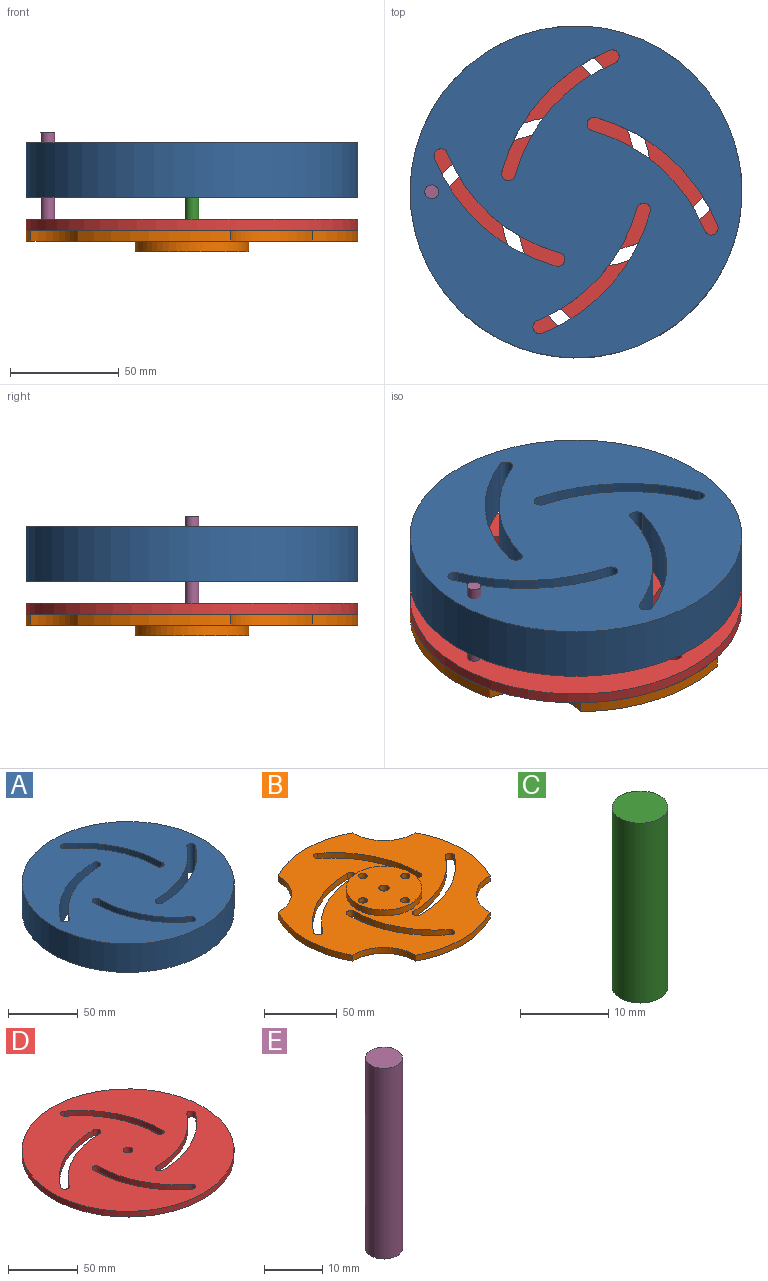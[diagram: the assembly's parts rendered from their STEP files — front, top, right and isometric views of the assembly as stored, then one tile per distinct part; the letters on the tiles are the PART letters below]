
ASSEMBLY  parts=5 mates=4
PART A: 19 faces, bbox 152.4x152.4x25 mm
  f0: plane 152.4x152.4mm, normal (0,0,1), area 16223.8mm2, adj f2,f3,f4,f5,f6,f7,f8,f9
  f1: plane 152.4x152.4mm, normal (0,0,-1), area 16223.8mm2, adj f2,f3,f4,f5,f6,f7,f8,f9
  f2: cylinder r=76.2mm len=152.4mm, axis (0,0,-1), area 11969.5mm2, adj f0,f1
  f3: cylinder r=83.46mm len=66.74mm, axis (0,0,1), area 1934.2mm2, adj f0,f1,f4,f6
  f4: cylinder r=3.18mm len=25mm, axis (0,0,1), area 250mm2, adj f0,f1,f3,f5
  f5: cylinder r=77.11mm len=61.66mm, axis (0,0,1), area 1787.1mm2, adj f0,f1,f4,f6
  f6: cylinder r=3.18mm len=25mm, axis (0,0,1), area 250.1mm2, adj f0,f1,f3,f5
  f7: cylinder r=77.11mm len=61.7mm, axis (0,0,1), area 1788mm2, adj f0,f1,f8,f10
  f8: cylinder r=3.18mm len=25mm, axis (0,0,1), area 246.9mm2, adj f0,f1,f7,f9
  f9: cylinder r=83.46mm len=66.78mm, axis (0,0,1), area 1935.2mm2, adj f0,f1,f8,f10
  f10: cylinder r=3.18mm len=25mm, axis (0,0,1), area 248.7mm2, adj f0,f1,f7,f9
  f11: cylinder r=77.11mm len=61.66mm, axis (0,0,1), area 1786.4mm2, adj f0,f1,f12,f14
  f12: cylinder r=3.17mm len=25mm, axis (0,0,1), area 249.4mm2, adj f0,f1,f11,f13
  f13: cylinder r=83.46mm len=66.74mm, axis (0,0,1), area 1933.5mm2, adj f0,f1,f12,f14
  f14: cylinder r=3.18mm len=25mm, axis (0,0,1), area 249.4mm2, adj f0,f1,f11,f13
  f15: cylinder r=77.11mm len=61.7mm, axis (0,0,1), area 1788mm2, adj f0,f1,f16,f18
  f16: cylinder r=3.18mm len=25mm, axis (0,0,1), area 251.3mm2, adj f0,f1,f15,f17
  f17: cylinder r=83.46mm len=66.78mm, axis (0,0,1), area 1935.2mm2, adj f0,f1,f16,f18
  f18: cylinder r=3.18mm len=25mm, axis (0,0,1), area 251mm2, adj f0,f1,f15,f17
PART B: 37 faces, bbox 152.4x152.4x10 mm
  f0: plane 152.4x152.4mm, normal (0,0,-1), area 14375.6mm2, adj f1,f2,f3,f5,f8,f9,f10,f11
  f1: cylinder r=76.2mm len=72.53mm, axis (0,0,-1), area 378mm2, adj f0,f4,f34,f35
  f2: cylinder r=76.2mm len=72.42mm, axis (0,0,-1), area 377.3mm2, adj f0,f4,f33,f34
  f3: cylinder r=76.2mm len=72.42mm, axis (0,0,-1), area 377.3mm2, adj f0,f4,f32,f33
  f4: plane 152.4x152.4mm, normal (0,0,1), area 12584.1mm2, adj f1,f2,f3,f5,f6,f8,f9,f10
  f5: cylinder r=76.2mm len=72.53mm, axis (0,0,-1), area 378mm2, adj f0,f4,f32,f35
  f6: cylinder r=26.12mm len=52.25mm, axis (0,0,-1), area 820.7mm2, adj f4,f7
  f7: plane 52.25x52.25mm, normal (0,0,1), area 1986.8mm2, adj f6,f24,f26,f28,f30,f36
  f8: cylinder r=83.46mm len=66.74mm, axis (0,0,1), area 386.8mm2, adj f0,f4,f9,f11
  f9: cylinder r=3.18mm len=5.72mm, axis (0,0,1), area 50mm2, adj f0,f4,f8,f10
  f10: cylinder r=77.11mm len=61.66mm, axis (0,0,1), area 357.4mm2, adj f0,f4,f9,f11
  f11: cylinder r=3.18mm len=6.35mm, axis (0,0,1), area 50mm2, adj f0,f4,f8,f10
  f12: cylinder r=77.11mm len=61.7mm, axis (0,0,1), area 357.6mm2, adj f0,f4,f13,f15
  f13: cylinder r=3.18mm len=6.35mm, axis (0,0,1), area 49.4mm2, adj f0,f4,f12,f14
  f14: cylinder r=83.46mm len=66.78mm, axis (0,0,1), area 387mm2, adj f0,f4,f13,f15
  f15: cylinder r=3.18mm len=5.71mm, axis (0,0,1), area 49.7mm2, adj f0,f4,f12,f14
  f16: cylinder r=77.11mm len=61.66mm, axis (0,0,1), area 357.3mm2, adj f0,f4,f17,f19
  f17: cylinder r=3.17mm len=6.35mm, axis (0,0,1), area 49.9mm2, adj f0,f4,f16,f18
  f18: cylinder r=83.46mm len=66.74mm, axis (0,0,1), area 386.7mm2, adj f0,f4,f17,f19
  f19: cylinder r=3.18mm len=5.71mm, axis (0,0,1), area 49.9mm2, adj f0,f4,f16,f18
  f20: cylinder r=77.11mm len=61.7mm, axis (0,0,1), area 357.6mm2, adj f0,f4,f21,f23
  f21: cylinder r=3.18mm len=6.35mm, axis (0,0,1), area 50.3mm2, adj f0,f4,f20,f22
  f22: cylinder r=83.46mm len=66.78mm, axis (0,0,1), area 387mm2, adj f0,f4,f21,f23
  f23: cylinder r=3.18mm len=5.74mm, axis (0,0,1), area 50.2mm2, adj f0,f4,f20,f22
  f24: cylinder r=3.08mm len=6.67mm, axis (0,0,-1), area 128.8mm2, adj f7,f25
  f25: cone r=3.08mm half-angle=30deg, axis (0,0,-1), area 97.7mm2, adj f0,f24
  f26: cylinder r=3.08mm len=6.67mm, axis (0,0,-1), area 128.8mm2, adj f7,f27
  f27: cone r=3.08mm half-angle=30deg, axis (0,0,-1), area 97.7mm2, adj f0,f26
  f28: cylinder r=3.08mm len=6.67mm, axis (0,0,-1), area 128.8mm2, adj f7,f29
  f29: cone r=3.08mm half-angle=30deg, axis (0,0,-1), area 97.7mm2, adj f0,f28
  f30: cylinder r=3.08mm len=6.67mm, axis (0,0,-1), area 128.8mm2, adj f7,f31
  f31: cone r=3.08mm half-angle=30deg, axis (0,0,-1), area 97.7mm2, adj f0,f30
  f32: cylinder r=30mm len=30.76mm, axis (0,0,-1), area 243.2mm2, adj f0,f3,f4,f5
  f33: cylinder r=30.11mm len=30.93mm, axis (0,0,-1), area 244.7mm2, adj f0,f2,f3,f4
  f34: cylinder r=30mm len=30.76mm, axis (0,0,-1), area 243.2mm2, adj f0,f1,f2,f4
  f35: cylinder r=30mm len=30.76mm, axis (0,0,-1), area 243.2mm2, adj f0,f1,f4,f5
  f36: cylinder r=3.5mm len=10mm, axis (0,0,-1), area 220mm2, adj f0,f7
PART C: 3 faces, bbox 6.4x6.4x25 mm
  f0: cylinder r=3.17mm len=25mm, axis (0,0,-1), area 498.7mm2, adj f1,f2
  f1: plane 6.35x6.35mm, normal (0,0,1), area 31.7mm2, adj f0
  f2: plane 6.35x6.35mm, normal (0,0,-1), area 31.7mm2, adj f0
PART D: 20 faces, bbox 152.4x152.4x5 mm
  f0: plane 152.4x152.4mm, normal (0,0,1), area 16185.3mm2, adj f2,f3,f4,f5,f6,f7,f8,f9
  f1: plane 152.4x152.4mm, normal (0,0,-1), area 16185.3mm2, adj f2,f3,f4,f5,f6,f7,f8,f9
  f2: cylinder r=76.2mm len=152.4mm, axis (0,0,-1), area 2393.9mm2, adj f0,f1
  f3: cylinder r=83.46mm len=66.74mm, axis (0,0,1), area 386.8mm2, adj f0,f1,f4,f6
  f4: cylinder r=3.18mm len=5.72mm, axis (0,0,1), area 50mm2, adj f0,f1,f3,f5
  f5: cylinder r=77.11mm len=61.66mm, axis (0,0,1), area 357.4mm2, adj f0,f1,f4,f6
  f6: cylinder r=3.18mm len=6.35mm, axis (0,0,1), area 50mm2, adj f0,f1,f3,f5
  f7: cylinder r=77.11mm len=61.7mm, axis (0,0,1), area 357.6mm2, adj f0,f1,f8,f10
  f8: cylinder r=3.18mm len=6.35mm, axis (0,0,1), area 49.4mm2, adj f0,f1,f7,f9
  f9: cylinder r=83.46mm len=66.78mm, axis (0,0,1), area 387mm2, adj f0,f1,f8,f10
  f10: cylinder r=3.18mm len=5.71mm, axis (0,0,1), area 49.7mm2, adj f0,f1,f7,f9
  f11: cylinder r=77.11mm len=61.66mm, axis (0,0,1), area 357.3mm2, adj f0,f1,f12,f14
  f12: cylinder r=3.17mm len=6.35mm, axis (0,0,1), area 49.9mm2, adj f0,f1,f11,f13
  f13: cylinder r=83.46mm len=66.74mm, axis (0,0,1), area 386.7mm2, adj f0,f1,f12,f14
  f14: cylinder r=3.18mm len=5.71mm, axis (0,0,1), area 49.9mm2, adj f0,f1,f11,f13
  f15: cylinder r=77.11mm len=61.7mm, axis (0,0,1), area 357.6mm2, adj f0,f1,f16,f18
  f16: cylinder r=3.18mm len=6.35mm, axis (0,0,1), area 50.3mm2, adj f0,f1,f15,f17
  f17: cylinder r=83.46mm len=66.78mm, axis (0,0,1), area 387mm2, adj f0,f1,f16,f18
  f18: cylinder r=3.18mm len=5.74mm, axis (0,0,1), area 50.2mm2, adj f0,f1,f15,f17
  f19: cylinder r=3.5mm len=7mm, axis (0,0,-1), area 110mm2, adj f0,f1
PART E: 3 faces, bbox 6.4x6.4x40 mm
  f0: cylinder r=3.17mm len=40mm, axis (0,0,-1), area 798mm2, adj f1,f2
  f1: plane 6.35x6.35mm, normal (0,0,1), area 31.7mm2, adj f0
  f2: plane 6.35x6.35mm, normal (0,0,-1), area 31.7mm2, adj f0
PLACE A rot(axis=(0.13,0.99,0),180deg) t=(-15.71,4.25,3.71)mm
PLACE B rot(axis=(0.99,-0.13,0),180deg) t=(-15.71,4.25,-36.29)mm
PLACE C rot(axis=(0,0,-1),15deg) t=(-15.71,4.25,-46.29)mm
PLACE D rot(axis=(0,0,-1),180deg) t=(-15.71,4.25,-36.29)mm
PLACE E t=(-81.92,4.24,-31.29)mm
MATE fastened C.f0 <-> A.f2  axis (0,0,-1) through (-15.71,4.25,-21.29)mm
MATE fastened C.f0 <-> B.f6  axis (0,0,-1) through (-15.71,4.25,-46.29)mm
MATE revolute D.f2 <-> B.f36  axis (0,0,-1) through (-15.71,4.25,-36.29)mm
MATE pin_slot E.f0 <-> D.f4  axis (0,0,-1) through (-81.92,4.24,-31.29)mm
